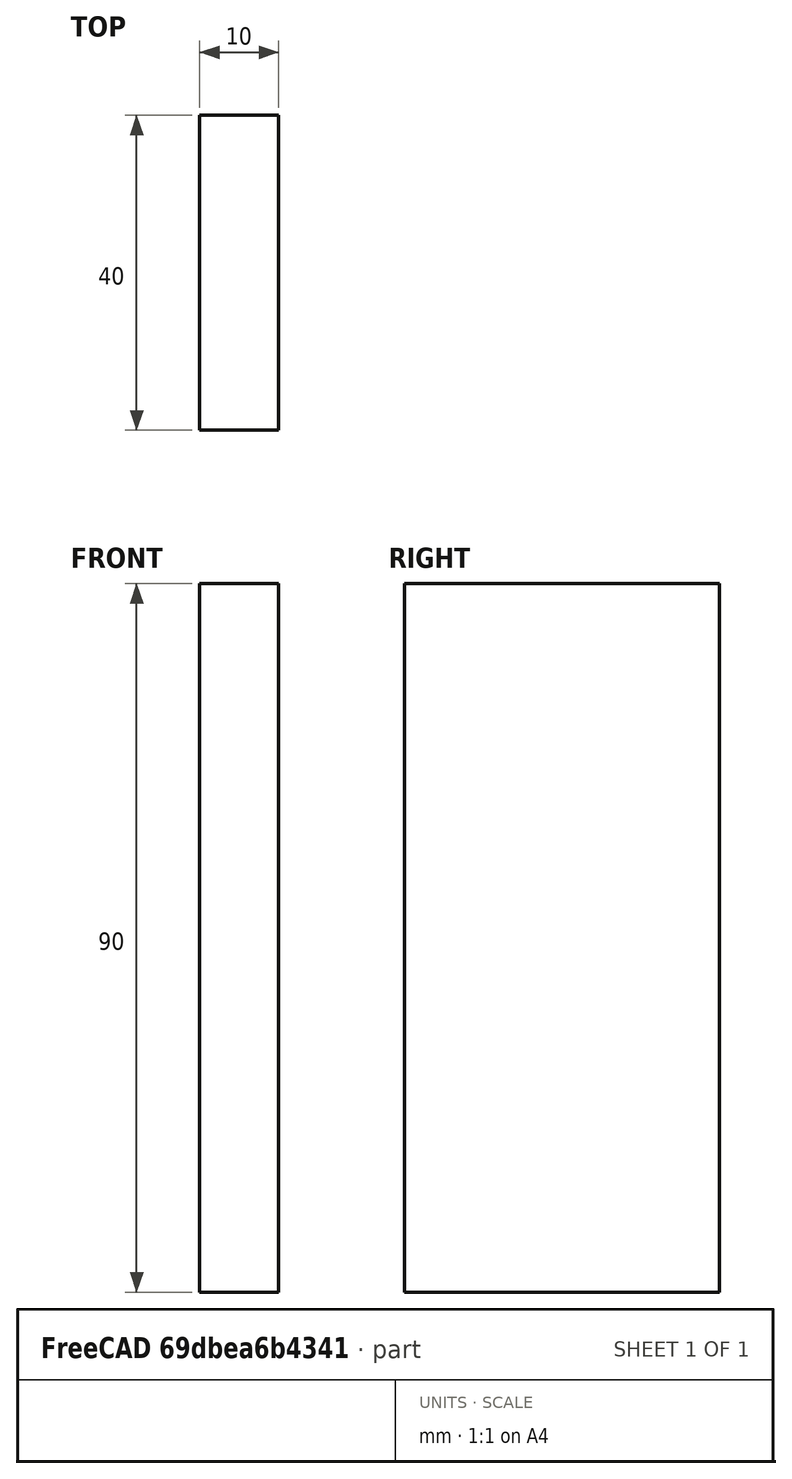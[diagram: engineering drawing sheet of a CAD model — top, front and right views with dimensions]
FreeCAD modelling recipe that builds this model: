
FCSTD DOCUMENT  (FreeCAD 0.17R13217 (Git))
Label: 01-Monolito
License: All rights reserved
LicenseURL: http://en.wikipedia.org/wiki/All_rights_reserved
objects: Sketcher::SketchObject×1, PartDesign::Pad×1, PartDesign::Body×1
note: 4 computed .brp shape members not serialized (recipe doc carries the construction recipe); baked Part::Feature solids carry a one-line shape summary decoded from their .brp

FEATURE [Sketcher::SketchObject] Sketch
  MapMode = 5
  Support = -> [XY_Plane]
  sketch-geometry (4):
    g0: LineSegment StartX=0 StartY=0 StartZ=0 EndX=0 EndY=40 EndZ=0
    g1: LineSegment StartX=0 StartY=40 StartZ=0 EndX=10 EndY=40 EndZ=0
    g2: LineSegment StartX=10 StartY=40 StartZ=0 EndX=10 EndY=0 EndZ=0
    g3: LineSegment StartX=10 StartY=0 StartZ=0 EndX=0 EndY=0 EndZ=0
  constraints (11):
    c: Coincident(g0,g1)
    c: Coincident(g0,g3)
    c: Coincident(g1,g2)
    c: Coincident(g2,g3)
    c: Horizontal(g3)
    c: Horizontal(g1)
    c: Vertical(g0)
    c: Vertical(g2)
    c: DistanceX(g3,g3) = 10
    c: DistanceY(g2,g2) = 40
    c: Coincident(g0,g-1)
FEATURE [PartDesign::Pad] Pad
  Length = 90
  Length2 = 100
  Profile = -> Sketch
  Refine = true
  Type = 0
FEATURE [PartDesign::Body] Body
  Group = -> [Sketch,Pad]
  Origin = -> Origin
  Tip = -> Pad
